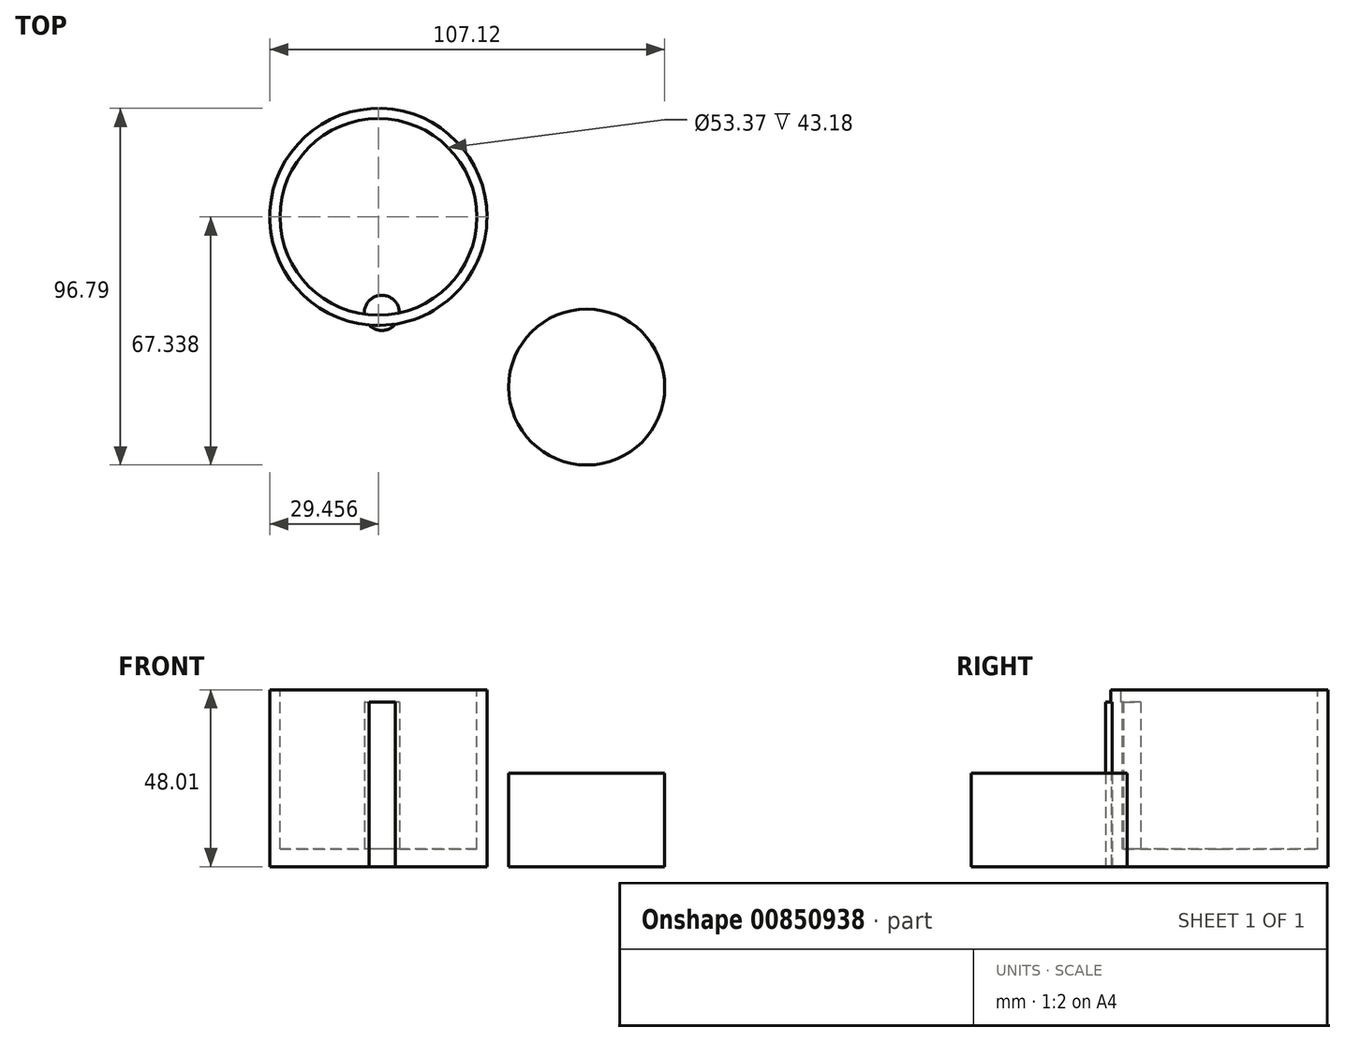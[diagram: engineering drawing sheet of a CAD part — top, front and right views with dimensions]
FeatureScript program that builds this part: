
annotation { "Feature Type Name" : "Feature", "Feature Type Description" : "" }
export const myFeature = defineFeature(function(context is Context, id is Id, definition is map)
    precondition{}
    {
        {
            var Q0;
            Q0=qCreatedBy(makeId("Top.planeOp"),FACE);
            var sketch = newSketch(context, id + "F0", { "sketchPlane" : qUnion([Q0])});
            skCircle(sketch, "E0", {"center": v(-14.3, 10.12) * mm, "radius": 29.45 * mm});
            skSolve(sketch);
        }
        {
            var Q0;
            Q0 = qSketchRegion(id + "F0", true);
            extrude(context, id + "F1", {"entities" : qUnion([Q0]), "depth" : 48 * mm, "offsetDistance" : 25.4 * mm});
        }
        {
            var Q0;
            Q0=makeQuery(id+"F1.opExtrude","CAP_FACE",FACE,{"disambiguationData":[OSD([sQuery(id+"F0.wireOp",EDGE,"E0")])],"isStart":false});
            var sketch = newSketch(context, id + "F2", { "sketchPlane" : qUnion([Q0])});
            skCircle(sketch, "E1", {"center": v(-14.3, 10.12) * mm, "radius": 26.68 * mm});
            skSolve(sketch);
        }
        {
            var Q0;
            Q0 = qSketchRegion(id + "F2", true);
            extrude(context, id + "F3", {"entities" : qUnion([Q0]), "operationType" : NewBodyOperationType.REMOVE, "oppositeDirection" : true, "depth" : 43.18 * mm, "offsetDistance" : 25.4 * mm});
        }
        {
            var Q0;
            Q0=makeQuery(id+"F1.opExtrude","CAP_FACE",FACE,{"disambiguationData":[OSD([sQuery(id+"F0.wireOp",EDGE,"E0")])],"isStart":true});
            var sketch = newSketch(context, id + "F4", { "sketchPlane" : qUnion([Q0])});
            skCircle(sketch, "E2", {"center": v(-14.3, -10.12) * mm, "radius": 21.66 * mm});
            skSolve(sketch);
        }
        {
            var Q0;
            Q0=qCreatedBy(makeId("Top.planeOp"),FACE);
            var sketch = newSketch(context, id + "F5", { "sketchPlane" : qUnion([Q0])});
            skCircle(sketch, "E3", {"center": v(-13.37, -15.93) * mm, "radius": 4.77 * mm});
            skSolve(sketch);
        }
        {
            var Q0;
            Q0 = qSketchRegion(id + "F5", true);
            extrude(context, id + "F6", {"entities" : qUnion([Q0]), "operationType" : NewBodyOperationType.ADD, "depth" : 44.7 * mm, "offsetDistance" : 25.4 * mm});
        }
        {
            var Q0;
            Q0 = qSketchRegion(id + "F4", true);
            extrude(context, id + "F7", {"entities" : qUnion([Q0]), "operationType" : NewBodyOperationType.ADD, "depth" : 25.4 * mm, "offsetDistance" : 25.4 * mm});
        }
        {
            var Q0;
            Q0=qCreatedBy(makeId("Top.planeOp"),FACE);
            var sketch = newSketch(context, id + "F8", { "sketchPlane" : qUnion([Q0])});
            skCircle(sketch, "E4", {"center": v(-14.9, 8.26) * mm, "radius": 56.12 * mm});
            skSolve(sketch);
        }
        {
            var Q0;
            Q0 = qSketchRegion(id + "F8", true);
            extrude(context, id + "F9", {"entities" : qUnion([Q0]), "operationType" : NewBodyOperationType.REMOVE, "oppositeDirection" : true, "depth" : 44.45 * mm, "offsetDistance" : 25.4 * mm});
        }
        {
            var Q0;
            Q0=qCreatedBy(makeId("Top.planeOp"),FACE);
            var sketch = newSketch(context, id + "F10", { "sketchPlane" : qUnion([Q0])});
            skCircle(sketch, "E5", {"center": v(42.2, -36.06) * mm, "radius": 21.16 * mm});
            skSolve(sketch);
        }
        {
            var Q0;
            Q0 = qSketchRegion(id + "F10", true);
            extrude(context, id + "F11", {"entities" : qUnion([Q0]), "depth" : 25.4 * mm, "offsetDistance" : 25.4 * mm});
        }
    });
